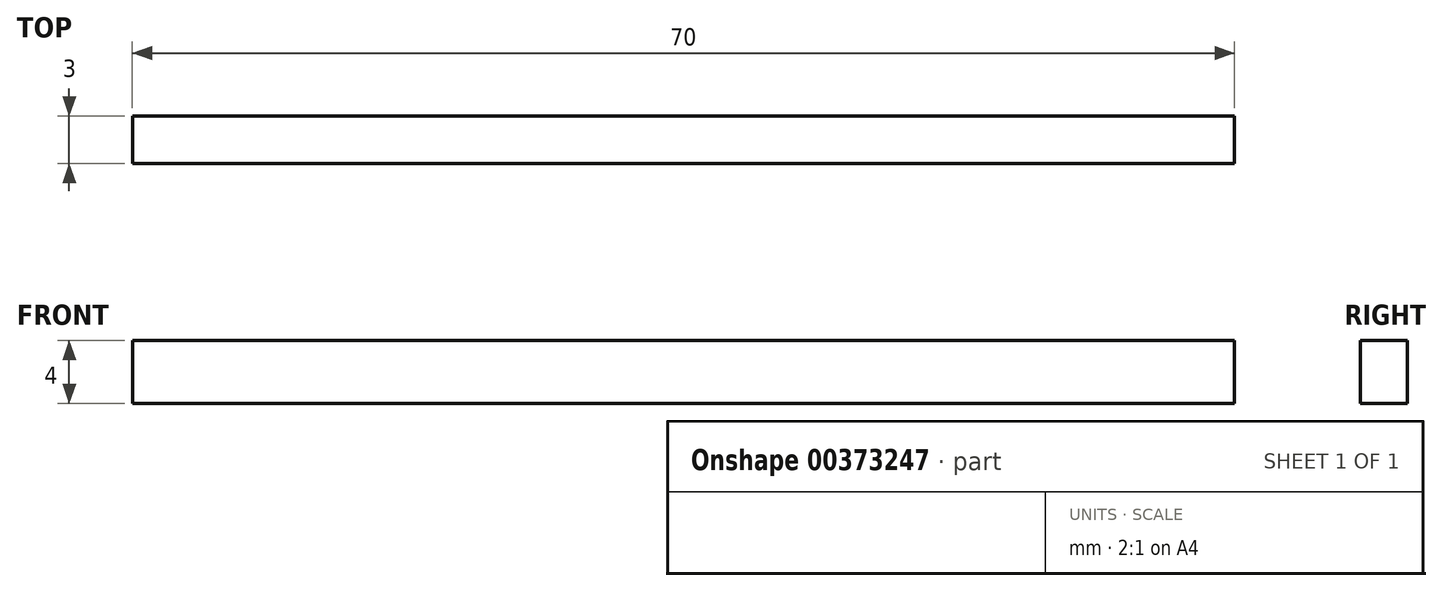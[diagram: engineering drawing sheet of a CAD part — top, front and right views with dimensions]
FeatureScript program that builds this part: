
annotation { "Feature Type Name" : "Feature", "Feature Type Description" : "" }
export const myFeature = defineFeature(function(context is Context, id is Id, definition is map)
    precondition{}
    {
        {
            var Q0;
            Q0=qCreatedBy(makeId("Front.planeOp"),FACE);
            var sketch = newSketch(context, id + "F0", { "sketchPlane" : qUnion([Q0])});
            skLineSegment(sketch, "E0.bottom", {"start": v(-1.3, 3.15) * mm, "end": v(68.7, 3.15) * mm});
            skLineSegment(sketch, "E0.top", {"start": v(-1.3, -0.85) * mm, "end": v(68.7, -0.85) * mm});
            skLineSegment(sketch, "E0.left", {"start": v(-1.3, 3.15) * mm, "end": v(-1.3, -0.85) * mm});
            skLineSegment(sketch, "E0.right", {"start": v(68.7, 3.15) * mm, "end": v(68.7, -0.85) * mm});
            skSolve(sketch);
        }
        {
            var Q0;
            Q0=qSketchRegion(id+"F0",true);
            extrude(context, id + "F1", {"entities" : qUnion([Q0]), "depth" : 3 * mm});
        }
    });
